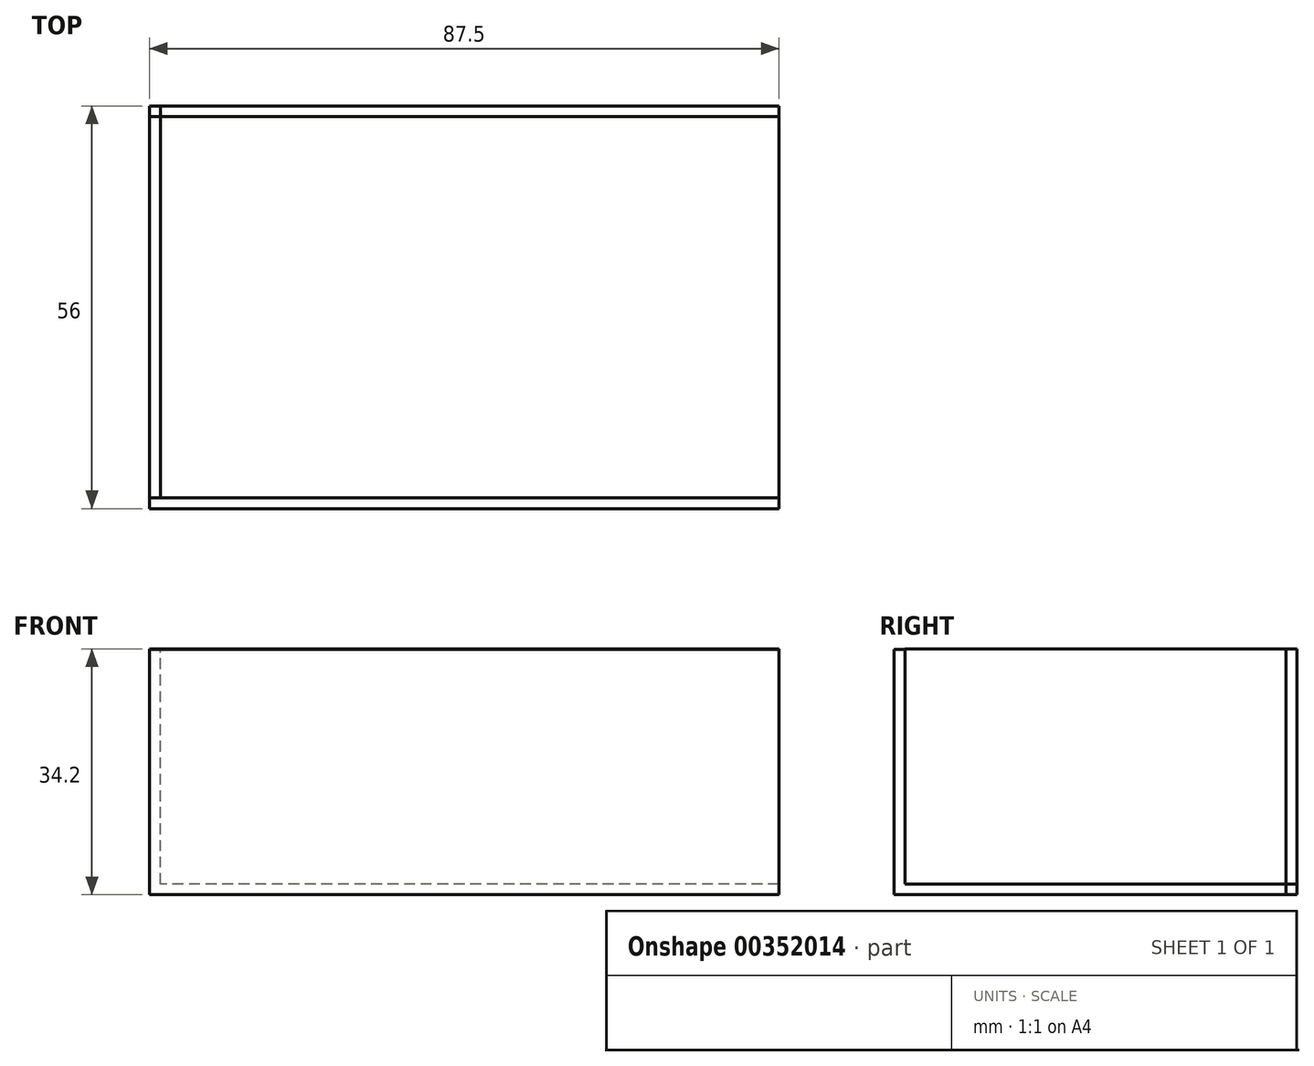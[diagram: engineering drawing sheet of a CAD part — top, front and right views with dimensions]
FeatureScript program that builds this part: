
annotation { "Feature Type Name" : "Feature", "Feature Type Description" : "" }
export const myFeature = defineFeature(function(context is Context, id is Id, definition is map)
    precondition{}
    {
        {
            var Q0;
            Q0=qCreatedBy(makeId("Top.planeOp"),FACE);
            var sketch = newSketch(context, id + "F0", { "sketchPlane" : qUnion([Q0])});
            skLineSegment(sketch, "E0.bottom", {"start": v(43, 26.5) * mm, "end": v(-43, 26.5) * mm});
            skLineSegment(sketch, "E0.top", {"start": v(43, -26.5) * mm, "end": v(-43, -26.5) * mm});
            skLineSegment(sketch, "E0.left", {"start": v(43, 26.5) * mm, "end": v(43, -26.5) * mm});
            skLineSegment(sketch, "E0.right", {"start": v(-43, 26.5) * mm, "end": v(-43, -26.5) * mm});
            skPoint(sketch, "E0.middle", {"position": v(0, 0) * mm});
            skSolve(sketch);
        }
        {
            var Q0;
            Q0=makeQuery(id+"F0.imprint","IMPRINT",FACE,{"disambiguationData":[TD([[makeQuery(id+"F0.imprint","IMPRINT",EDGE,{"derivedFrom":sQuery(id+"F0.wireOp",EDGE,"E0.bottom")}),1.0]])]});
            extrude(context, id + "F1", {"entities" : qUnion([Q0]), "depth" : 1.5 * mm});
        }
        {
            var Q0;
            Q0=makeQuery(id+"F1.opExtrude","SWEPT_FACE",FACE,{"disambiguationData":[OSD([sQuery(id+"F0.wireOp",EDGE,"E0.right")])]});
            var sketch = newSketch(context, id + "F2", { "sketchPlane" : qUnion([Q0])});
            skLineSegment(sketch, "E1.bottom", {"start": v(-26.5, 0) * mm, "end": v(26.5, 0) * mm});
            skLineSegment(sketch, "E1.top", {"start": v(-26.5, 34.2) * mm, "end": v(26.5, 34.2) * mm});
            skLineSegment(sketch, "E1.left", {"start": v(-26.5, 0) * mm, "end": v(-26.5, 34.2) * mm});
            skLineSegment(sketch, "E1.right", {"start": v(26.5, 0) * mm, "end": v(26.5, 34.2) * mm});
            skSolve(sketch);
        }
        {
            var Q0;
            {var subQ0=sQuery(id+"F2.wireOp",EDGE,"E1.top");Q0=makeQuery(id+"F2.imprint","IMPRINT",FACE,{"disambiguationData":[TD([[makeQuery(id+"F2.imprint","IMPRINT",EDGE,{"derivedFrom":subQ0}),-1.0]])]});}
            var Q1;
            {var subQ0=sQuery(id+"F2.wireOp",EDGE,"E1.bottom");Q1=makeQuery(id+"F2.imprint","IMPRINT",FACE,{"disambiguationData":[TD([[makeQuery(id+"F2.imprint","IMPRINT",EDGE,{"derivedFrom":subQ0}),1.0]])]});}
            extrude(context, id + "F3", {"entities" : qUnion([Q0, Q1]), "operationType" : NewBodyOperationType.ADD, "depth" : 1.5 * mm});
        }
        {
            var Q0;
            Q0=makeQuery(id+"F3.boolean.opBoolean","MERGE",FACE,{"derivedFrom":[makeQuery(id+"F1.opExtrude","SWEPT_FACE",FACE,{"disambiguationData":[OSD([sQuery(id+"F0.wireOp",EDGE,"E0.bottom")])]}),makeQuery(id+"F3.opExtrude","SWEPT_FACE",FACE,{"disambiguationData":[OSD([sQuery(id+"F2.wireOp",EDGE,"E1.left")])]})]});
            var sketch = newSketch(context, id + "F4", { "sketchPlane" : qUnion([Q0])});
            skLineSegment(sketch, "E2.bottom", {"start": v(-43, 0) * mm, "end": v(44.5, 0) * mm});
            skLineSegment(sketch, "E2.top", {"start": v(-43, 34.2) * mm, "end": v(44.5, 34.2) * mm});
            skLineSegment(sketch, "E2.left", {"start": v(-43, 0) * mm, "end": v(-43, 34.2) * mm});
            skLineSegment(sketch, "E2.right", {"start": v(44.5, 0) * mm, "end": v(44.5, 34.2) * mm});
            skSolve(sketch);
        }
        {
            var Q0;
            {var subQ4=makeQuery(id+"F1.opExtrude","CAP_EDGE",EDGE,{"disambiguationData":[OSD([sQuery(id+"F0.wireOp",EDGE,"E0.bottom")])],"isStart":false});Q0=makeQuery(id+"F4.imprint","IMPRINT",FACE,{"disambiguationData":[TD([[makeQuery(id+"F4.imprint","IMPRINT",EDGE,{"derivedFrom":subQ4}),1.0]])]});}
            extrude(context, id + "F5", {"entities" : qUnion([Q0]), "depth" : 1.5 * mm});
        }
        {
            var Q0;
            Q0=makeQuery(id+"F3.boolean.opBoolean","MERGE",FACE,{"derivedFrom":[makeQuery(id+"F1.opExtrude","SWEPT_FACE",FACE,{"disambiguationData":[OSD([sQuery(id+"F0.wireOp",EDGE,"E0.bottom")])]}),makeQuery(id+"F3.opExtrude","SWEPT_FACE",FACE,{"disambiguationData":[OSD([sQuery(id+"F2.wireOp",EDGE,"E1.left")])]})]});
            extrude(context, id + "F6", {"entities" : qUnion([Q0]), "depth" : 1.5 * mm});
        }
        {
            var Q0;
            Q0=makeQuery(id+"F3.boolean.opBoolean","MERGE",FACE,{"derivedFrom":[makeQuery(id+"F1.opExtrude","SWEPT_FACE",FACE,{"disambiguationData":[OSD([sQuery(id+"F0.wireOp",EDGE,"E0.top")])]}),makeQuery(id+"F3.opExtrude","SWEPT_FACE",FACE,{"disambiguationData":[OSD([sQuery(id+"F2.wireOp",EDGE,"E1.right")])]})]});
            var sketch = newSketch(context, id + "F7", { "sketchPlane" : qUnion([Q0])});
            skLineSegment(sketch, "E3.bottom", {"start": v(-44.5, 0) * mm, "end": v(43, 0) * mm});
            skLineSegment(sketch, "E3.top", {"start": v(-44.5, 34.1) * mm, "end": v(43, 34.1) * mm});
            skLineSegment(sketch, "E3.left", {"start": v(-44.5, 0) * mm, "end": v(-44.5, 34.1) * mm});
            skLineSegment(sketch, "E3.right", {"start": v(43, 0) * mm, "end": v(43, 34.1) * mm});
            skSolve(sketch);
        }
        {
            var Q0;
            {var subQ5=makeQuery(id+"F1.opExtrude","CAP_EDGE",EDGE,{"disambiguationData":[OSD([sQuery(id+"F0.wireOp",EDGE,"E0.top")])],"isStart":false});Q0=makeQuery(id+"F7.imprint","IMPRINT",FACE,{"disambiguationData":[TD([[makeQuery(id+"F7.imprint","IMPRINT",EDGE,{"derivedFrom":subQ5}),-1.0]])]});}
            var Q1;
            {var subQ6=sQuery(id+"F7.wireOp",EDGE,"E3.bottom");Q1=makeQuery(id+"F7.imprint","IMPRINT",FACE,{"disambiguationData":[TD([[makeQuery(id+"F7.imprint","IMPRINT",EDGE,{"derivedFrom":subQ6}),-1.0]])]});}
            extrude(context, id + "F8", {"entities" : qUnion([Q0, Q1]), "operationType" : NewBodyOperationType.ADD, "depth" : 1.5 * mm});
        }
    });
